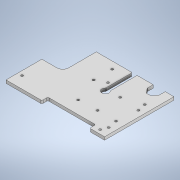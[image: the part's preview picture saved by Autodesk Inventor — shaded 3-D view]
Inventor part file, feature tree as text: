
AUTODESK INVENTOR PART (.ipt)
format: ipt  version: 2021 (Build 250183000, 183)  size: 268,288 bytes
history: native  units: mm
features: sketch x11, extrude x6, hole x5, fillet x4, projected_geometry x1
ambient origin geometry x8: Origin, YZ Plane, XZ Plane, XY Plane, X Axis, Y Axis, Z Axis, Center Point
bodies: Solid1 (feature_tree)
feature tree (27):
  extrude  "Extrusion1"  Depth=116.2mm
  hole  "Hole1"  [1 undecoded]
  extrude  "Extrusion2"  Depth=50.0mm
  fillet  "Fillet1"  Radius=47.0mm
  extrude  "Extrusion3"  Depth=72.25mm
  hole  "Hole2"  [1 undecoded]
  hole  "Hole3"  [1 undecoded]
  extrude  "Extrusion4"  Depth=5.0mm TaperAngle=0.0deg
  fillet  "Fillet2"  Radius=2.0mm
  hole  "Hole4"  [1 undecoded]
  extrude  "Extrusion5"  Depth=5.0mm TaperAngle=0.0deg
  fillet  "Fillet3"  Radius=91.5mm
  extrude  "Extrusion6"  Depth=8.0mm
  fillet  "Fillet4"  Radius=13.0mm
  hole  "Hole5"  [1 undecoded]
  sketch  "Sketch1"  dims[d0=130.0mm d1=116.2mm]
  sketch  "Sketch2"  dims[d2=5.0mm d3=0.0mm d4=10.0mm]
  sketch  "Sketch3"  dims[d5=16.7mm d6=50.0mm d7=47.0mm]
  sketch  "Sketch4"  dims[d8=4.5mm d9=72.25mm]
  sketch  "Sketch5"  dims[d10=98.25mm]
  sketch  "Sketch6"  dims[d11=3.8mm d12=6.0mm d13=4.0mm d14=2.0mm d15=90.0deg d16=8.0mm d17=20.594885mm d18=10.0mm]
  sketch  "Sketch7"  dims[d19=25.0mm d20=25.0mm]
  sketch  "Sketch8"  dims[d21=2.0mm d22=5.0mm d23=0.0mm d24=2.0mm]
  sketch  "Sketch9"  dims[d25=12.0mm d26=65.75mm]
  sketch  "Sketch10"  dims[d27=67.1mm d28=5.0mm d29=0.0mm d30=91.5mm]
  projected_geometry  "Projected Loop1"
  sketch  "Sketch11"  dims[d31=12.0mm d32=43.0mm d33=3.8mm d34=6.0mm d35=4.0mm d36=2.0mm d37=90.0deg d38=8.0mm d39=20.594885mm d40=13.0mm d41=36.0mm d42=84.0mm d43=3.8mm d44=6.0mm d45=4.0mm d46=2.0mm d47=90.0deg d48=8.0mm d49=20.594885mm d50=44.0mm d51=46.0mm d52=84.0mm d53=14.0mm d54=6.7mm d55=60.0mm d56=5.0mm d57=35.0mm d58=0.0mm d59=10.0mm d60=19.5mm d61=7.25mm d62=3.8mm d63=6.0mm d64=4.0mm d65=2.0mm d66=90.0deg d67=8.0mm d68=20.594885mm d69=24.65mm d70=20.0mm d71=36.0mm d72=10.0mm d73=8.0mm d74=0.0mm d75=0.0mm d76=2.0mm d77=8.0mm d78=0.0mm d79=0.0mm d80=2.0mm d81=75.5mm d82=35.0mm d83=85.0mm d84=3.8mm d85=6.0mm d86=4.0mm d87=2.0mm d88=90.0deg d89=8.0mm d90=20.594885mm]
note: 5 required parameter values undecoded (feature->parameter linkage not recoverable at this tier; creation-order binding heuristic only, values carry confidence <= 0.55)
